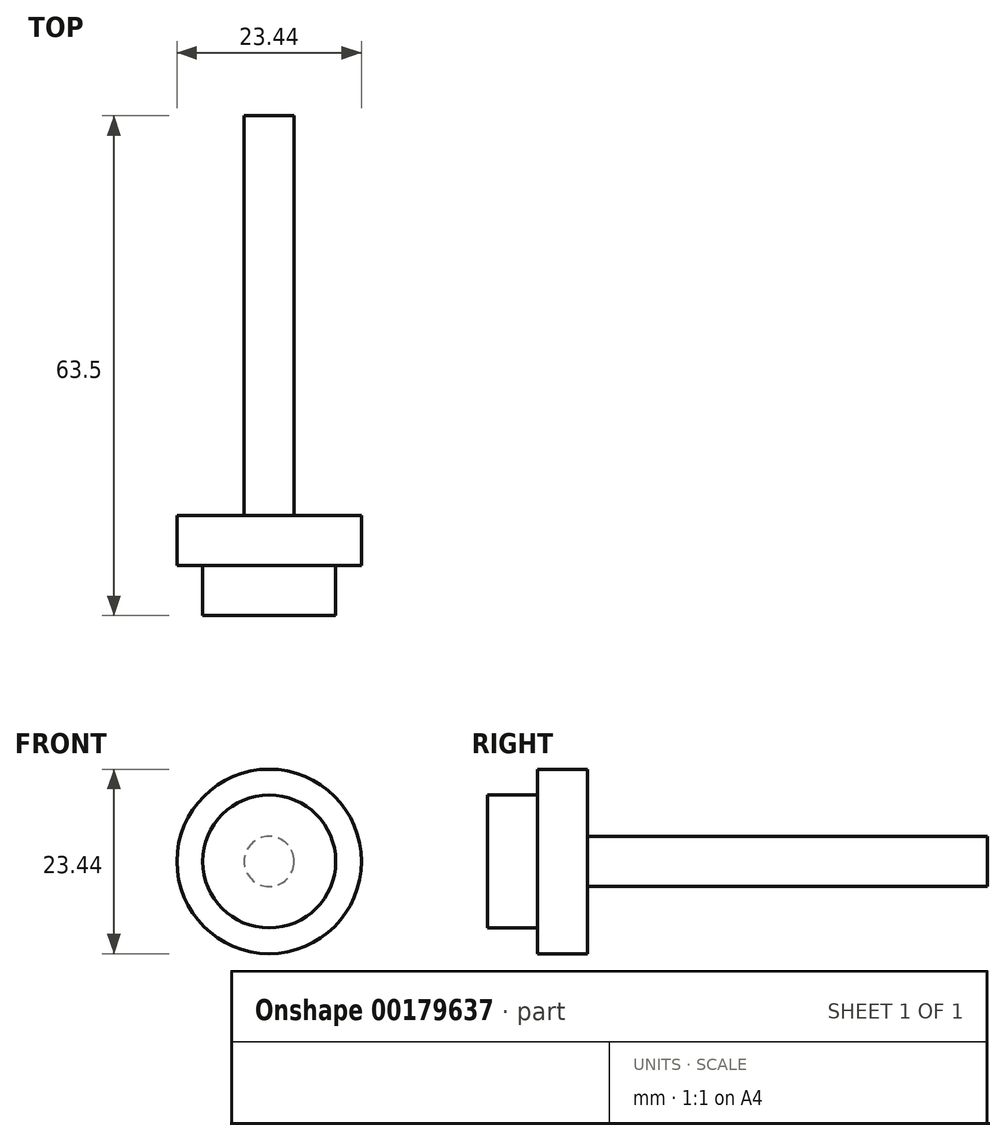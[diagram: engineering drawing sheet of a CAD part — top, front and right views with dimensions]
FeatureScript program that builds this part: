
annotation { "Feature Type Name" : "Feature", "Feature Type Description" : "" }
export const myFeature = defineFeature(function(context is Context, id is Id, definition is map)
    precondition{}
    {
        {
            var Q0;
            Q0=qCreatedBy(makeId("Front.planeOp"),FACE);
            var sketch = newSketch(context, id + "F0", { "sketchPlane" : qUnion([Q0])});
            skCircle(sketch, "E0", {"center": v(0, 0) * mm, "radius": 8.45 * mm});
            skSolve(sketch);
        }
        {
            var Q0;
            Q0 = qSketchRegion(id + "F0", true);
            extrude(context, id + "F1", {"entities" : qUnion([Q0]), "depth" : 6.35 * mm});
        }
        {
            var Q0;
            Q0=qCreatedBy(makeId("Front.planeOp"),FACE);
            var sketch = newSketch(context, id + "F2", { "sketchPlane" : qUnion([Q0])});
            skCircle(sketch, "E1", {"center": v(0, 0) * mm, "radius": 11.72 * mm});
            skSolve(sketch);
        }
        {
            var Q0;
            Q0 = qSketchRegion(id + "F2", true);
            extrude(context, id + "F3", {"entities" : qUnion([Q0]), "operationType" : NewBodyOperationType.ADD, "oppositeDirection" : true, "depth" : 6.35 * mm});
        }
        {
            var Q0;
            Q0=qCreatedBy(makeId("Front.planeOp"),FACE);
            var sketch = newSketch(context, id + "F4", { "sketchPlane" : qUnion([Q0])});
            skCircle(sketch, "E2", {"center": v(0, 0) * mm, "radius": 3.18 * mm});
            skSolve(sketch);
        }
        {
            var Q0;
            Q0 = qSketchRegion(id + "F4", true);
            extrude(context, id + "F5", {"entities" : qUnion([Q0]), "operationType" : NewBodyOperationType.ADD, "oppositeDirection" : true, "depth" : 57.15 * mm});
        }
    });
